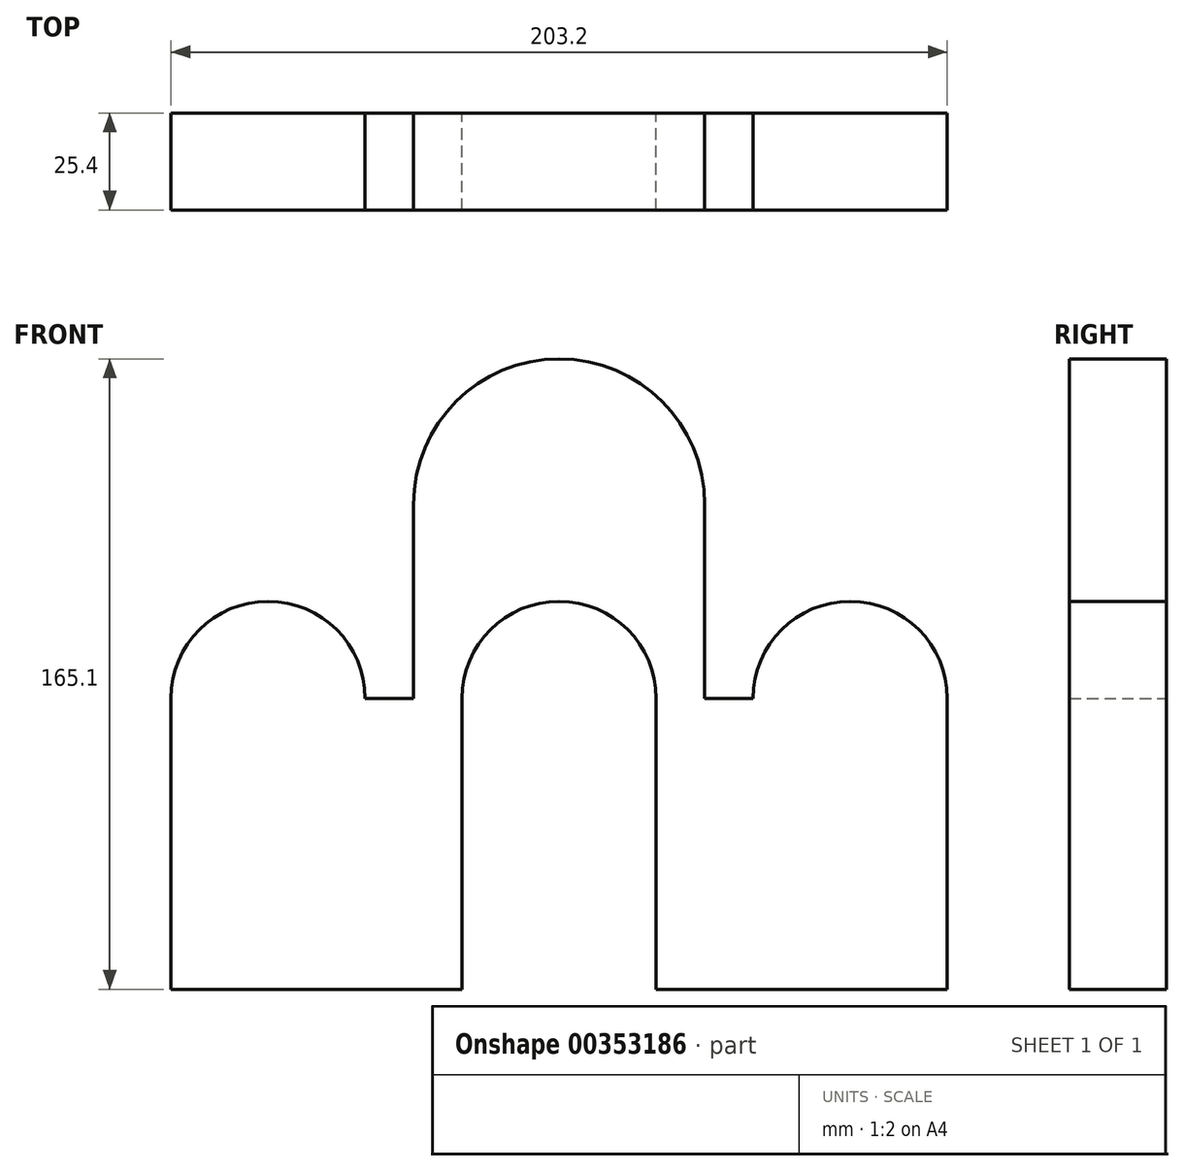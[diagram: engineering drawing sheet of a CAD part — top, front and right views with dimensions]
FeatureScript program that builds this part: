
annotation { "Feature Type Name" : "Feature", "Feature Type Description" : "" }
export const myFeature = defineFeature(function(context is Context, id is Id, definition is map)
    precondition{}
    {
        {
            var Q0;
            Q0=qCreatedBy(makeId("Front.planeOp"),FACE);
            var sketch = newSketch(context, id + "F0", { "sketchPlane" : qUnion([Q0])});
            skLineSegment(sketch, "E0", {"start": v(-27.2, -24.57) * mm, "end": v(49, -24.57) * mm});
            skLineSegment(sketch, "E1", {"start": v(49, -24.57) * mm, "end": v(49, 51.63) * mm});
            skLineSegment(sketch, "E2", {"start": v(-27.2, -24.57) * mm, "end": v(-27.2, 51.63) * mm});
            skArc(sketch, "E3", {"start": v(-27.2, 51.63) * mm, "mid": v(-1.8, 77.03) * mm, "end": v(23.6, 51.63) * mm});
            skLineSegment(sketch, "E4", {"start": v(-27.2, 51.63) * mm, "end": v(23.6, 51.63) * mm, "construction": true});
            skArc(sketch, "E5", {"start": v(49, 51.63) * mm, "mid": v(56.44, 69.6) * mm, "end": v(74.4, 77.03) * mm});
            skLineSegment(sketch, "E6", {"start": v(74.4, 51.63) * mm, "end": v(74.4, 85.74) * mm, "construction": true});
            skLineSegment(sketch, "E7", {"start": v(23.6, 51.63) * mm, "end": v(36.3, 51.63) * mm});
            skLineSegment(sketch, "E8", {"start": v(36.3, 51.63) * mm, "end": v(36.3, 102.43) * mm});
            skArc(sketch, "E9", {"start": v(36.3, 102.43) * mm, "mid": v(48.37, 130.25) * mm, "end": v(76.92, 140.45) * mm});
            skArc(sketch, "E10.MirrorCS", {"start": v(112.5, 102.43) * mm, "mid": v(100.44, 130.25) * mm, "end": v(71.9, 140.45) * mm});
            skLineSegment(sketch, "E11.MirrorCS", {"start": v(112.5, 51.63) * mm, "end": v(112.5, 102.43) * mm});
            skLineSegment(sketch, "E12.MirrorCS", {"start": v(125.2, 51.63) * mm, "end": v(112.5, 51.63) * mm});
            skArc(sketch, "E13.MirrorCS", {"start": v(176, 51.63) * mm, "mid": v(150.6, 77.03) * mm, "end": v(125.2, 51.63) * mm});
            skLineSegment(sketch, "E14.MirrorCS", {"start": v(176, -24.57) * mm, "end": v(176, 51.63) * mm});
            skLineSegment(sketch, "E15.MirrorCS", {"start": v(176, -24.57) * mm, "end": v(99.8, -24.57) * mm});
            skLineSegment(sketch, "E16.MirrorCS", {"start": v(99.8, -24.57) * mm, "end": v(99.8, 51.63) * mm});
            skArc(sketch, "E17.MirrorCS", {"start": v(99.8, 51.63) * mm, "mid": v(92.37, 69.6) * mm, "end": v(74.4, 77.03) * mm});
            skSolve(sketch);
        }
        {
            var Q0;
            Q0 = qSketchRegion(id + "F0", true);
            extrude(context, id + "F1", {"entities" : qUnion([Q0]), "depth" : 25.4 * mm});
        }
    });
